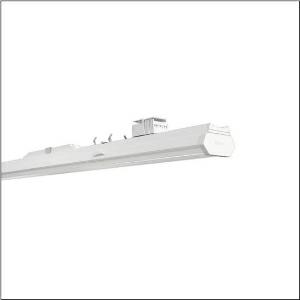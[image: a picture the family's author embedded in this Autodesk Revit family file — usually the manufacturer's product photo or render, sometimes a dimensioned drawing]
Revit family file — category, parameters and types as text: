
# Revit family: licross_r__11_protected_ho_51tp11dn4exr_f87d
name_source: partatom
category: Lighting Fixtures
units: mm (PartAtom-declared; Revit-internal decimal feet)

## family parameters
Cut with Voids When Loaded = No
Host = Face
Light Source = No
Part Type = Normal
Room Calculation Point = No
Round Connector Dimension = Use Diameter
Shared = No

## types (1)
- --- (1 x LED, 14140 lm, 84.2 W, 4000K)
    Apparent Load = 84 VA
    CIE Flux Codes = 84 94 98 99 100
    Color Rendering = 80
    Color Temperature = 4000K
    Default Elevation = 1800 mm
    Description = Licross® 11 Protected HOluminaire insert, length: 1.500mm, width: 90mm, height: 101mm, LED rated luminous flux: 14.140lm, light colour: 840, control gear: DALI 2, control gear: ECG DALI, with plug, 5-pole, with phase selection, mains connection: 220..240V, AC, 50/60Hz, halogen-free wiring, primary optical cover: cover, of PMMA, light emission: direct with ceiling illumination distribution, protection rating (complete): IP64, insulation class (complete): insulation class I (protective earthing), certification: CE, ENEC, VDE, protection symbol: D if used in an environment with conductive dust loads with corresponding accessories, permissible ambient temperature for indoor applications: -25..+35°C, reducing of maximum allowable ambient temperature of 5°C with ceiling mounting, corresponds to IFS (International Featured Standards) requirements for safety and quality in the food industry, packaging unit: 1 piece
    Height = 92 mm
    Lamp = 1 x LED
    Lamp Light Flux = 14140 lm
    Lamp Power = 84.2 W
    Lamp count = 1
    Length = 1500 mm
    Luminous efficacy = 168 lm/W
    Manufacturer = Siteco
    ModVariant = No
    Model = 51TP11DN4EXR
    Mounting Place = Ceiling
    Mounting Type = Pendant
    Number of Poles = 1
    OnlyDefault = Yes
    Power Factor = 1
    Product Name = Licross® 11 Protected HO
    Product group = luminaire insert
    ProductGroupID = 902
    Protection Class = Protection class I
    Protection Degree = IP 64
    RLX_Detail_Level = 1
    RlxData = <blob elided: 24061 chars, md5=d8d48002>
    Socket = socket
    Standby Power = 0 W
    System Light Flux = 14140 lm
    System Power = 84 W
    Type Comments = factory setting: luminous flux: 100 % | dim-lin: 254 | 475 mA
    Type Image = l_1256148.jpg
    URL = http://relux.com
    VarID = @adj_137733
    Voltage = 0 V
    Weight = 0.00 kg
    Width = 88 mm

## geometry (parser evidence)
native form markers: Blend x4, Sweep x13
no freeform markers — native parametric forms only
